# Revit family: Hager-VEGAD-Surface_mounted-IP41-With_Cover-With_DIN-Hosted-BE-fr
name_source: partatom
category: Electrical Equipment
units: mm (PartAtom-declared; Revit-internal decimal feet)

## family parameters
Cut with Voids When Loaded = No
Host = Face
Maintain Annotation Orientation = Yes
Panel Configuration = Two Columns, Circuits Across
Part Type = Panelboard
Room Calculation Point = No
Round Connector Dimension = Use Diameter
Shared = No

## types (14) — shared parameters
BC_MODEL_ID = 1546997
BC_OBJECT_ID = 513430
BC_OBJECT_VERSION = #5
Code hager = ADD-EC000214_EU
EF000003 - Type de montage = Apparent
EF000007 - Couleur = Blanc
EF000008 - Largeur = 550 mm  [stored 1.80446 ft]
EF000024 - Résistant aux UV = No
EF000049 - Profondeur = 193 mm  [stored 0.633202 ft]
EF000116 - Numéro RAL = 9010
EF000218 - Profondeur d'encastrement = 193 mm  [stored 0.633202 ft]
EF000846 - Largeur de montage = 550 mm  [stored 1.80446 ft]
EF001062 - Finition CEM = No
EF001088 - Possibilité de montage en saillie = Yes
EF001134 - Avec Rail DIN = Yes
EF002950 - Largeur dans les unités de partition = 24
EF004462 - Type de fermeture = Autre
EF005474 - Classe de protection (IP) = IP41
EF006306 - Avec serrure = No
EF015776 - Borne de mise à la terre = Yes
EF015777 - Borne à conducteur neutre = No
EF015941 - Porte pour transmission du signal = No
ETIM class code = EC000214
ETIM class name = Small distribution board
HG000001-nombre de colonnes = 1
HG000002-avec porte = Yes
HG000003-Gamme = VEGAD
HG000005-Epaisseur = 2 mm  [stored 0.00656168 ft]
HG000006-Encastré = No
HG000009-Porte à double battant = No
HG000010-Portes asymétriques = No
HG000012-Angle de pivotement de la porte = 90.00°
HG000013-Porte à gauche = No
HG000014-Porte à droite = Yes
HG000015-Visibilité de l'emprise de la porte = Yes
HG000016-Visibilité de la porte 3D = Yes
HG000017-Distance entre pôles = 18 mm  [stored 0.0590551 ft]
HG000060-RAL-number = 9010
HG000099-ID modèle Onfly = 507532
HGEF0002950-largeur en nombre de modules = 24
Manufacturer = Hager
Name = VEGAD-Surface_mounted-IP41-With_Cover-With_DIN-BE
Name BIM&CO = Electricity
Name hager = ADD_Enclosures_EC000214
Uniformat = Low Tension Service & Dist.
Uniformat code = D501001
zero-valued in all types: Default Elevation, EF001131 - Profondeur intérieure, HG000007-Nombre de colonnes vides

## per-type parameters (varying)
| type | BC_VARIANT_ID | EF000040 - Hauteur | EF000118 - Avec plaque de montage | EF000266 - Nombre de rangées | EF000332 - Hauteur d'encastrement | EF006244 - Couvercle/porte transparent(e) | EF009212 - Finition du couvercle | HG000004-Référence fabricant | HG000008-Nombre de rangées vides | HG000011-Rangées du bas vides | HGEF000266-Nombre de rangées |
| VEGAD-Surface_mounted_W550_H450_D193_24_Modular_Spacing-FD22BN | 1173743 | 450 mm  [stored 1.47638 ft] | No | 2 | 450 mm  [stored 1.47638 ft] | No | Fermé | FD22BN | 0 | No | 2 |
| VEGAD-Surface_mounted_W550_H450_D193_24_Modular_Spacing-FD22CN | 1173744 | 450 mm  [stored 1.47638 ft] | No | 2 | 450 mm  [stored 1.47638 ft] | Yes | Avec échancrure | FD22CN | 0 | No | 2 |
| VEGAD-Surface_mounted_W550_H600_D193_24_Modular_Spacing-FD32BN | 1173745 | 600 mm | No | 3 | 600 mm | No | Fermé | FD32BN | 0 | No | 3 |
| VEGAD-Surface_mounted_W550_H600_D193_24_Modular_Spacing-FD32CN | 1173746 | 600 mm | No | 3 | 600 mm | Yes | Fermé | FD32CN | 0 | No | 3 |
| VEGAD-Surface_mounted_W550_H750_D193_24_Modular_Spacing-FD42BMN | 1173747 | 750 mm  [stored 2.46063 ft] | Yes | 4 | 750 mm  [stored 2.46063 ft] | No | Fermé | FD42BMN | 3 | Yes | 4 |
| VEGAD-Surface_mounted_W550_H750_D193_24_Modular_Spacing-FD42BN | 1173748 | 750 mm  [stored 2.46063 ft] | No | 4 | 750 mm  [stored 2.46063 ft] | No | Fermé | FD42BN | 0 | No | 4 |
| VEGAD-Surface_mounted_W550_H750_D193_24_Modular_Spacing-FD42CN | 1173749 | 750 mm  [stored 2.46063 ft] | No | 4 | 750 mm  [stored 2.46063 ft] | Yes | Avec échancrure | FD42CN | 0 | No | 4 |
| VEGAD-Surface_mounted_W550_H900_D193_24_Modular_Spacing-FD52BMN | 1173750 | 900 mm  [stored 2.95276 ft] | Yes | 5 | 900 mm  [stored 2.95276 ft] | No | Fermé | FD52BMN | 3 | Yes | 5 |
| VEGAD-Surface_mounted_W550_H900_D193_24_Modular_Spacing-FD52BN | 1173751 | 900 mm  [stored 2.95276 ft] | No | 5 | 900 mm  [stored 2.95276 ft] | No | Fermé | FD52BN | 0 | No | 5 |
| VEGAD-Surface_mounted_W550_H900_D193_24_Modular_Spacing-FD52CN | 1173752 | 900 mm  [stored 2.95276 ft] | No | 5 | 900 mm  [stored 2.95276 ft] | Yes | Avec échancrure | FD52CN | 0 | No | 5 |
| VEGAD-Surface_mounted_W550_H1050_D193_24_Modular_Spacing-FD62BN | 1173753 | 1050 mm | No | 6 | 1050 mm | No | Fermé | FD62BN | 0 | No | 6 |
| VEGAD-Surface_mounted_W550_H1050_D193_24_Modular_Spacing-FD62CN | 1173755 | 1050 mm | No | 6 | 1050 mm | Yes | Avec échancrure | FD62CN | 0 | No | 6 |
| VEGAD-Surface_mounted_W550_H1200_D193_24_Modular_Spacing-FD72BN | 1173757 | 1200 mm  [stored 3.93701 ft] | No | 7 | 1200 mm  [stored 3.93701 ft] | No | Fermé | FD72BN | 0 | No | 7 |
| VEGAD-Surface_mounted_W550_H1200_D193_24_Modular_Spacing-FD72CN | 1173759 | 1200 mm  [stored 3.93701 ft] | No | 7 | 1200 mm  [stored 3.93701 ft] | Yes | Avec échancrure | FD72CN | 0 | No | 7 |

note: column(s) folded — value = type name in every type: Reference

note: [stored X ft] marks values corroborated as IEEE doubles in the binary element streams (Revit-internal decimal feet)

## geometry (parser evidence)
native form markers: Sweep x17
no freeform markers — native parametric forms only
